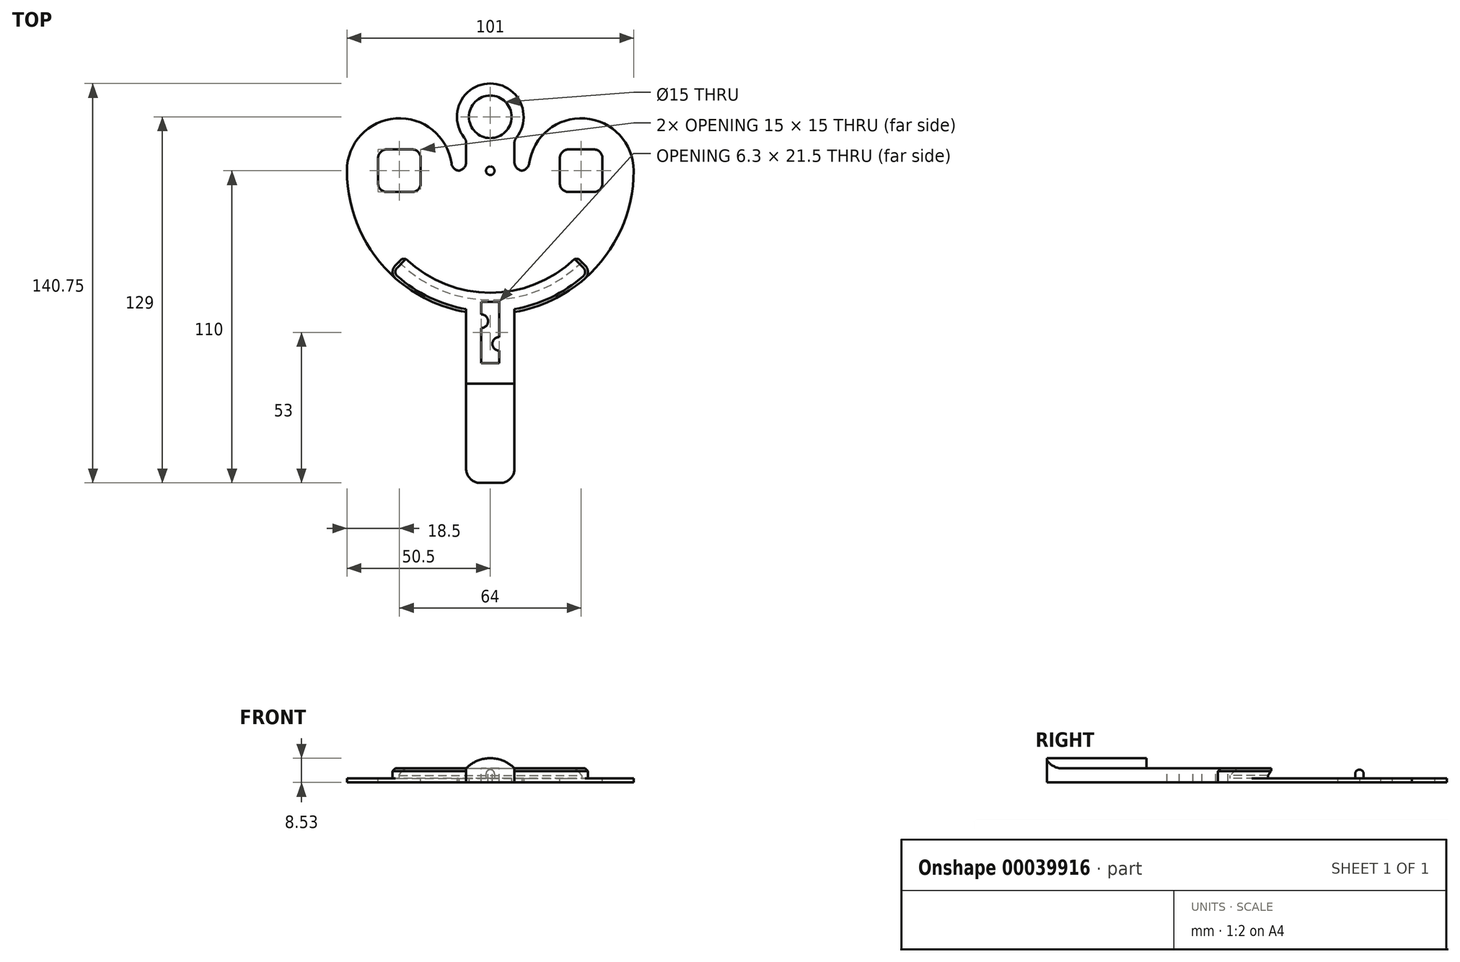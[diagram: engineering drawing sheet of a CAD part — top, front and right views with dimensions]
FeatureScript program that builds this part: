
annotation { "Feature Type Name" : "Feature", "Feature Type Description" : "" }
export const myFeature = defineFeature(function(context is Context, id is Id, definition is map)
    precondition{}
    {
        {
            var Q0;
            Q0=qCreatedBy(makeId("Top.planeOp"),FACE);
            var sketch = newSketch(context, id + "F0", { "sketchPlane" : qUnion([Q0])});
            skLineSegment(sketch, "E0", {"start": v(0, 35) * mm, "end": v(0, -35) * mm, "construction": true});
            skLineSegment(sketch, "E1", {"start": v(-8.5, -40) * mm, "end": v(-8.5, -110) * mm});
            skLineSegment(sketch, "E2", {"start": v(-8.5, -110) * mm, "end": v(0, -110) * mm});
            skLineSegment(sketch, "E3.MirrorCS", {"start": v(8.5, -40) * mm, "end": v(8.5, -110) * mm});
            skLineSegment(sketch, "E4.MirrorCS", {"start": v(8.5, -110) * mm, "end": v(0, -110) * mm});
            skEllipse(sketch, "E5.0", {"center": v(0, 0) * mm, "majorRadius": 67.5 * mm, "minorRadius": 35 * mm, "majorAxis": v(1, 0), "construction": true});
            skCircle(sketch, "E6.0", {"center": v(-32, 0) * mm, "radius": 17.5 * mm, "construction": true});
            skCircle(sketch, "E7.0", {"center": v(32, 0) * mm, "radius": 17.5 * mm, "construction": true});
            skLineSegment(sketch, "E8", {"start": v(0, -110) * mm, "end": v(0, -40) * mm, "construction": true});
            skLineSegment(sketch, "E9", {"start": v(0, -35) * mm, "end": v(0, -40) * mm, "construction": true});
            skLineSegment(sketch, "E10", {"start": v(-8.5, -40) * mm, "end": v(8.5, -40) * mm});
            skSolve(sketch);
        }
        {
            var Q0;
            Q0=qSketchRegion(id+"F0",true);
            extrude(context, id + "F1", {"entities" : qUnion([Q0]), "depth" : 5 * mm});
        }
        {
            var Q0;
            Q0=makeQuery(id+"F1.opExtrude","CAP_FACE",FACE,{"disambiguationData":[OSD([sQuery(id+"F0.wireOp",EDGE,"7391e9a9-ae98-415e-9696-a7713fd930ae"),sQuery(id+"F0.wireOp",EDGE,"7767e17a-6af5-4bc8-a544-19a58f6916b8"),sQuery(id+"F0.wireOp",EDGE,"E1"),sQuery(id+"F0.wireOp",EDGE,"E2"),sQuery(id+"F0.wireOp",EDGE,"69639bf5-fd83-4191-99ff-23f08a1ee2360.MirrorCS"),sQuery(id+"F0.wireOp",EDGE,"e829f9c4-7dbb-4f23-9f44-d63990e1826a0.MirrorCS"),sQuery(id+"F0.wireOp",EDGE,"E3.MirrorCS"),sQuery(id+"F0.wireOp",EDGE,"E4.MirrorCS")])],"isStart":false});
            var sketch = newSketch(context, id + "F2", { "sketchPlane" : qUnion([Q0])});
            skLineSegment(sketch, "E11", {"start": v(0, 0) * mm, "end": v(0, -57) * mm, "construction": true});
            skLineSegment(sketch, "E12.rect.bottom", {"start": v(3.15, -67.75) * mm, "end": v(-3.15, -67.75) * mm});
            skLineSegment(sketch, "E12.rect.top", {"start": v(3.15, -46.25) * mm, "end": v(-3.15, -46.25) * mm});
            skLineSegment(sketch, "E12.rect.left", {"start": v(3.15, -67.75) * mm, "end": v(3.15, -46.25) * mm, "construction": true});
            skLineSegment(sketch, "E12.rect.right", {"start": v(-3.15, -67.75) * mm, "end": v(-3.15, -46.25) * mm, "construction": true});
            skPoint(sketch, "E12.rect.middle", {"position": v(0, -57) * mm});
            skLineSegment(sketch, "E13", {"start": v(-3.15, -46.25) * mm, "end": v(-3.15, -50.6) * mm});
            skArc(sketch, "E14", {"start": v(-3.15, -55.4) * mm, "mid": v(-0.75, -53) * mm, "end": v(-3.15, -50.6) * mm});
            skLineSegment(sketch, "E15", {"start": v(-3.15, -53) * mm, "end": v(-3.15, -46.25) * mm, "construction": true});
            skLineSegment(sketch, "E16", {"start": v(-3.15, -55.4) * mm, "end": v(-3.15, -67.75) * mm});
            skLineSegment(sketch, "E17", {"start": v(3.15, -67.75) * mm, "end": v(3.15, -63.4) * mm});
            skArc(sketch, "E18", {"start": v(3.15, -58.6) * mm, "mid": v(0.75, -61) * mm, "end": v(3.15, -63.4) * mm});
            skLineSegment(sketch, "E19", {"start": v(3.15, -58.6) * mm, "end": v(3.15, -46.25) * mm});
            skLineSegment(sketch, "E20", {"start": v(-3.15, -53) * mm, "end": v(-3.15, -57) * mm, "construction": true});
            skLineSegment(sketch, "E21", {"start": v(-3.15, -57) * mm, "end": v(0, -57) * mm, "construction": true});
            skLineSegment(sketch, "E22", {"start": v(3.15, -61) * mm, "end": v(3.15, -57) * mm, "construction": true});
            skSolve(sketch);
        }
        {
            var Q0;
            Q0=qSketchRegion(id+"F2",true);
            extrude(context, id + "F3", {"entities" : qUnion([Q0]), "operationType" : NewBodyOperationType.REMOVE, "endBound" : BoundingType.THROUGH_ALL, "oppositeDirection" : true, "depth" : 140 * mm});
        }
        {
            var Q0;
            Q0=makeQuery(id+"F1.opExtrude","SWEPT_FACE",FACE,{"disambiguationData":[OSD([sQuery(id+"F0.wireOp",EDGE,"E2"),sQuery(id+"F0.wireOp",EDGE,"E4.MirrorCS")])]});
            var sketch = newSketch(context, id + "F4", { "sketchPlane" : qUnion([Q0])});
            skLineSegment(sketch, "E23", {"start": v(-8.5, 5) * mm, "end": v(8.5, 5) * mm});
            skArc(sketch, "E24", {"start": v(8.5, 5) * mm, "mid": v(0, 8.53) * mm, "end": v(-8.5, 5) * mm});
            skSolve(sketch);
        }
        {
            var Q0;
            Q0=qSketchRegion(id+"F4",true);
            extrude(context, id + "F5", {"entities" : qUnion([Q0]), "operationType" : NewBodyOperationType.ADD, "oppositeDirection" : true, "depth" : 35 * mm});
        }
        {
            var Q0;
            Q0=makeQuery(id+"F5.opExtrude","CAP_EDGE",EDGE,{"disambiguationData":[OSD([sQuery(id+"F4.wireOp",EDGE,"E23")])],"isStart":false});
            var Q1;
            Q1=makeQuery(id+"FVXrfRP8fz1N6uW_1.boolean.opBoolean","INTERSECT",EDGE,{"derivedFrom":[makeQuery(id+"F1.opExtrude","SWEPT_FACE",FACE,{"disambiguationData":[OSD([sQuery(id+"F0.wireOp",EDGE,"E1")])]}),makeQuery(id+"FVXrfRP8fz1N6uW_1.opExtrude","SWEPT_FACE",FACE,{"disambiguationData":[OSD([sQuery(id+"FPdbJcEM4c8p8f5_1.wireOp",EDGE,"055e796a-4696-4a1f-8bd5-7584a93b29ed.right")])]})]});
            var Q2;
            Q2=makeQuery(id+"FVXrfRP8fz1N6uW_1.boolean.opBoolean","INTERSECT",EDGE,{"derivedFrom":[makeQuery(id+"F1.opExtrude","SWEPT_FACE",FACE,{"disambiguationData":[OSD([sQuery(id+"F0.wireOp",EDGE,"E3.MirrorCS")])]}),makeQuery(id+"FVXrfRP8fz1N6uW_1.opExtrude","SWEPT_FACE",FACE,{"disambiguationData":[OSD([sQuery(id+"FPdbJcEM4c8p8f5_1.wireOp",EDGE,"055e796a-4696-4a1f-8bd5-7584a93b29ed.right")])]})]});
            var Q3;
            Q3=makeQuery(id+"F1.opExtrude","SWEPT_EDGE",EDGE,{"disambiguationData":[OSD([sQuery(id+"F0.wireOp",EDGE,"E1"),sQuery(id+"F0.wireOp",EDGE,"E2")])]});
            var Q4;
            Q4=makeQuery(id+"F1.opExtrude","SWEPT_EDGE",EDGE,{"disambiguationData":[OSD([sQuery(id+"F0.wireOp",EDGE,"E3.MirrorCS"),sQuery(id+"F0.wireOp",EDGE,"E4.MirrorCS")])]});
            fillet(context, id + "F6", {"entities" : qUnion([Q0, Q1, Q2, Q3, Q4]), "radius" : 5 * mm, "tangentPropagation" : true, "allowEdgeOverflow" : false});
        }
        {
            var Q0;
            Q0=qCreatedBy(makeId("Top.planeOp"),FACE);
            var sketch = newSketch(context, id + "F7", { "sketchPlane" : qUnion([Q0])});
            skCircle(sketch, "E25", {"center": v(0, 0) * mm, "radius": 32 * mm, "construction": true});
            skPoint(sketch, "E26.0", {"position": v(32, 0) * mm});
            skPoint(sketch, "E27.0", {"position": v(-8.5, -40) * mm});
            skPoint(sketch, "E28.0", {"position": v(8.5, -40) * mm});
            skLineSegment(sketch, "E29.bottom", {"start": v(-8.5, -40) * mm, "end": v(8.5, -40) * mm});
            skLineSegment(sketch, "E29.top", {"start": v(-8.5, 0) * mm, "end": v(8.5, 0) * mm, "construction": true});
            skLineSegment(sketch, "E29.left", {"start": v(-8.5, -40) * mm, "end": v(-8.5, 0) * mm});
            skLineSegment(sketch, "E29.right", {"start": v(8.5, -40) * mm, "end": v(8.5, 0) * mm});
            skLineSegment(sketch, "E30", {"start": v(0, 0) * mm, "end": v(0, 19) * mm, "construction": true});
            skCircle(sketch, "E31", {"center": v(0, 19) * mm, "radius": 7.5 * mm});
            skCircle(sketch, "E32", {"center": v(0, 19) * mm, "radius": 11.75 * mm});
            skLineSegment(sketch, "E33.top", {"start": v(-8.5, 10.9) * mm, "end": v(8.5, 10.9) * mm, "construction": true});
            skLineSegment(sketch, "E33.left", {"start": v(-8.5, 0) * mm, "end": v(-8.5, 10.9) * mm});
            skLineSegment(sketch, "E33.right", {"start": v(8.5, 0) * mm, "end": v(8.5, 10.9) * mm});
            skLineSegment(sketch, "E34", {"start": v(0, 7.25) * mm, "end": v(0, 11.5) * mm, "construction": true});
            skSolve(sketch);
        }
        {
            var Q0;
            Q0 = qSketchRegion(id + "F7", true);
            extrude(context, id + "F8", {"entities" : qUnion([Q0]), "operationType" : NewBodyOperationType.ADD, "depth" : 5 * mm});
        }
        {
            var Q0;
            Q0=makeQuery(id+"F8.boolean.opBoolean","MERGE",FACE,{"derivedFrom":[makeQuery(id+"F1.opExtrude","CAP_FACE",FACE,{"disambiguationData":[OSD([sQuery(id+"F0.wireOp",EDGE,"E1"),sQuery(id+"F0.wireOp",EDGE,"E2"),sQuery(id+"F0.wireOp",EDGE,"E3.MirrorCS"),sQuery(id+"F0.wireOp",EDGE,"E4.MirrorCS"),sQuery(id+"F0.wireOp",EDGE,"E10")])],"isStart":false}),makeQuery(id+"F8.opExtrude","CAP_FACE",FACE,{"disambiguationData":[OSD([sQuery(id+"F7.wireOp",EDGE,"E29.bottom"),sQuery(id+"F7.wireOp",EDGE,"E29.left"),sQuery(id+"F7.wireOp",EDGE,"E29.right"),sQuery(id+"F7.wireOp",EDGE,"d812d8d3-a707-410c-a5e6-c5c524671fea")])],"isStart":false})]});
            var sketch = newSketch(context, id + "F9", { "sketchPlane" : qUnion([Q0])});
            skCircle(sketch, "E35", {"center": v(0, 0) * mm, "radius": 45.5 * mm});
            skSolve(sketch);
        }
        {
            var Q0;
            Q0 = qSketchRegion(id + "F9", true);
            extrude(context, id + "F10", {"entities" : qUnion([Q0]), "operationType" : NewBodyOperationType.REMOVE, "oppositeDirection" : true, "depth" : 3.5 * mm});
        }
        {
            var Q0;
            Q0=qCreatedBy(makeId("Top.planeOp"),FACE);
            var sketch = newSketch(context, id + "F11", { "sketchPlane" : qUnion([Q0])});
            skCircle(sketch, "E36.0", {"center": v(0, 0) * mm, "radius": 45.5 * mm, "construction": true});
            skArc(sketch, "E37", {"start": v(-45.5, 0) * mm, "mid": v(0, -45.5) * mm, "end": v(45.5, 0) * mm, "construction": true});
            skArc(sketch, "E38.0", {"start": v(-50.5, 0) * mm, "mid": v(0, -50.5) * mm, "end": v(50.5, 0) * mm});
            skPoint(sketch, "E39.0", {"position": v(-32, 0) * mm});
            skArc(sketch, "E40", {"start": v(-13.5, 0) * mm, "mid": v(-32, 18.5) * mm, "end": v(-50.5, 0) * mm});
            skArc(sketch, "E41.MirrorCS", {"start": v(13.5, 0) * mm, "mid": v(32, 18.5) * mm, "end": v(50.5, 0) * mm});
            skLineSegment(sketch, "E42", {"start": v(-13.5, 0) * mm, "end": v(13.5, 0) * mm});
            skSolve(sketch);
        }
        {
            var Q0;
            Q0=makeQuery(id+"F11.imprint","IMPRINT",FACE,{"disambiguationData":[TD([[makeQuery(id+"F11.imprint","IMPRINT",EDGE,{"derivedFrom":sQuery(id+"F11.wireOp",EDGE,"E38.0")}),1.0]])]});
            extrude(context, id + "F12", {"entities" : qUnion([Q0]), "operationType" : NewBodyOperationType.ADD, "depth" : 1.5 * mm});
        }
        {
            var Q0;
            Q0=makeQuery(id+"F12.boolean.opBoolean","MERGE",FACE,{"derivedFrom":[makeQuery(id+"F10.boolean.opBoolean","COPY",FACE,{"derivedFrom":makeQuery(id+"F10.opExtrude","CAP_FACE",FACE,{"disambiguationData":[OSD([sQuery(id+"F9.wireOp",EDGE,"E35")])],"isStart":false})}),makeQuery(id+"F12.opExtrude","CAP_FACE",FACE,{"disambiguationData":[OSD([sQuery(id+"F11.wireOp",EDGE,"E38.0"),sQuery(id+"F11.wireOp",EDGE,"07fb357d-3f39-45c2-a34c-5d68cf75340c")])],"isStart":false})]});
            var sketch = newSketch(context, id + "F13", { "sketchPlane" : qUnion([Q0])});
            skLineSegment(sketch, "E43", {"start": v(-50.5, 0) * mm, "end": v(-50.5, 0) * mm});
            skArc(sketch, "E44.0", {"start": v(-32.17, -32.17) * mm, "mid": v(0, -45.5) * mm, "end": v(32.17, -32.17) * mm});
            skPoint(sketch, "E45.0", {"position": v(-8.5, -44.7) * mm});
            skArc(sketch, "E46", {"start": v(-35.7, -35.7) * mm, "mid": v(0, -50.5) * mm, "end": v(35.7, -35.7) * mm});
            skLineSegment(sketch, "E47", {"start": v(0, 0) * mm, "end": v(-35.7, -35.7) * mm, "construction": true});
            skLineSegment(sketch, "E48.MirrorCS", {"start": v(0, 0) * mm, "end": v(35.7, -35.7) * mm, "construction": true});
            skLineSegment(sketch, "E49", {"start": v(-35.7, -35.7) * mm, "end": v(-32.17, -32.17) * mm});
            skLineSegment(sketch, "E50", {"start": v(35.7, -35.7) * mm, "end": v(32.17, -32.17) * mm});
            skSolve(sketch);
        }
        {
            var Q0;
            Q0 = qSketchRegion(id + "F13", true);
            extrude(context, id + "F14", {"entities" : qUnion([Q0]), "operationType" : NewBodyOperationType.ADD, "depth" : 3.5 * mm});
        }
        {
            var Q0;
            Q0=makeQuery(id+"F14.opExtrude","CAP_VERTEX",VERTEX,{"disambiguationData":[OSD([sQuery(id+"F13.wireOp",EDGE,"E44.0"),sQuery(id+"F13.wireOp",EDGE,"E49")])],"isStart":false});
            var Q1;
            Q1=makeQuery(id+"F14.boolean.opBoolean","MERGE",EDGE,{"derivedFrom":[makeQuery(id+"F10.boolean.opBoolean","COPY",EDGE,{"derivedFrom":makeQuery(id+"F10.opExtrude","CAP_EDGE",EDGE,{"disambiguationData":[OSD([sQuery(id+"F9.wireOp",EDGE,"E35")])],"isStart":true})}),makeQuery(id+"F14.opExtrude","CAP_EDGE",EDGE,{"disambiguationData":[OSD([sQuery(id+"F13.wireOp",EDGE,"E44.0")])],"isStart":false})]});
            cPlane(context, id + "F15", {"entities" : qUnion([Q0, Q1]), "cplaneType" : CPlaneType.CURVE_POINT, "offset" : 150 * mm, "width" : 150 * mm, "height" : 150 * mm});
        }
        {
            var Q0;
            Q0=qCreatedBy(id+"F15.planeOp",FACE);
            var sketch = newSketch(context, id + "F16", { "sketchPlane" : qUnion([Q0])});
            skPoint(sketch, "E51.0", {"position": v(-45.5, 5) * mm});
            skLineSegment(sketch, "E52", {"start": v(-45.5, 5) * mm, "end": v(-45.5, 2.5) * mm});
            skLineSegment(sketch, "E53", {"start": v(-45.5, 2.5) * mm, "end": v(-43, 5) * mm});
            skLineSegment(sketch, "E54", {"start": v(-43, 5) * mm, "end": v(-45.5, 5) * mm});
            skSolve(sketch);
        }
        {
            var Q0;
            Q0=makeQuery(id+"F16.imprint","IMPRINT",FACE,{"disambiguationData":[TD([[makeQuery(id+"F16.imprint","IMPRINT",EDGE,{"derivedFrom":sQuery(id+"F16.wireOp",EDGE,"E52")}),1.0]])]});
            var Q1;
            Q1=makeQuery(id+"F14.boolean.opBoolean","MERGE",EDGE,{"derivedFrom":[makeQuery(id+"F10.boolean.opBoolean","COPY",EDGE,{"derivedFrom":makeQuery(id+"F10.opExtrude","CAP_EDGE",EDGE,{"disambiguationData":[OSD([sQuery(id+"F9.wireOp",EDGE,"E35")])],"isStart":true})}),makeQuery(id+"F14.opExtrude","CAP_EDGE",EDGE,{"disambiguationData":[OSD([sQuery(id+"F13.wireOp",EDGE,"E44.0")])],"isStart":false})]});
            sweep(context, id + "F17", {"operationType" : NewBodyOperationType.ADD, "profiles" : qUnion([Q0]), "path" : qUnion([Q1])});
        }
        {
            var Q0;
            Q0=makeQuery(id+"F12.boolean.opBoolean","MERGE",FACE,{"derivedFrom":[makeQuery(id+"F10.boolean.opBoolean","COPY",FACE,{"derivedFrom":makeQuery(id+"F10.opExtrude","CAP_FACE",FACE,{"disambiguationData":[OSD([sQuery(id+"F9.wireOp",EDGE,"E35")])],"isStart":false})}),makeQuery(id+"F12.opExtrude","CAP_FACE",FACE,{"disambiguationData":[OSD([sQuery(id+"F11.wireOp",EDGE,"E38.0"),sQuery(id+"F11.wireOp",EDGE,"E40"),sQuery(id+"F11.wireOp",EDGE,"E41.MirrorCS"),sQuery(id+"F11.wireOp",EDGE,"E42")])],"isStart":false})]});
            var sketch = newSketch(context, id + "F18", { "sketchPlane" : qUnion([Q0])});
            skLineSegment(sketch, "E55.rect.bottom", {"start": v(-24.5, -7.5) * mm, "end": v(-39.5, -7.5) * mm});
            skLineSegment(sketch, "E55.rect.top", {"start": v(-24.5, 7.5) * mm, "end": v(-39.5, 7.5) * mm});
            skLineSegment(sketch, "E55.rect.left", {"start": v(-24.5, -7.5) * mm, "end": v(-24.5, 7.5) * mm});
            skLineSegment(sketch, "E55.rect.right", {"start": v(-39.5, -7.5) * mm, "end": v(-39.5, 7.5) * mm});
            skPoint(sketch, "E55.rect.middle", {"position": v(-32, 0) * mm});
            skLineSegment(sketch, "E56.rect.bottom", {"start": v(24.5, -7.5) * mm, "end": v(39.5, -7.5) * mm});
            skLineSegment(sketch, "E56.rect.top", {"start": v(24.5, 7.5) * mm, "end": v(39.5, 7.5) * mm});
            skLineSegment(sketch, "E56.rect.left", {"start": v(24.5, -7.5) * mm, "end": v(24.5, 7.5) * mm});
            skLineSegment(sketch, "E56.rect.right", {"start": v(39.5, -7.5) * mm, "end": v(39.5, 7.5) * mm});
            skPoint(sketch, "E56.rect.middle", {"position": v(32, 0) * mm});
            skSolve(sketch);
        }
        {
            var Q0;
            Q0 = qSketchRegion(id + "F18", true);
            extrude(context, id + "F19", {"entities" : qUnion([Q0]), "operationType" : NewBodyOperationType.REMOVE, "endBound" : BoundingType.THROUGH_ALL, "oppositeDirection" : true, "depth" : 25 * mm});
        }
        {
            var Q0;
            Q0=makeQuery(id+"F2.imprint","IMPRINT",FACE,{"disambiguationData":[TD([[makeQuery(id+"F2.imprint","IMPRINT",EDGE,{"derivedFrom":sQuery(id+"F2.wireOp",EDGE,"E12.rect.bottom")}),-1.0]])]});
            extrude(context, id + "F20", {"entities" : qUnion([Q0]), "operationType" : NewBodyOperationType.REMOVE, "endBound" : BoundingType.THROUGH_ALL, "oppositeDirection" : true, "depth" : 25 * mm});
        }
        {
            var Q0;
            Q0=makeQuery(id+"F12.boolean.opBoolean","MERGE",FACE,{"derivedFrom":[makeQuery(id+"F10.boolean.opBoolean","COPY",FACE,{"derivedFrom":makeQuery(id+"F10.opExtrude","CAP_FACE",FACE,{"disambiguationData":[OSD([sQuery(id+"F9.wireOp",EDGE,"E35")])],"isStart":false})}),makeQuery(id+"F12.opExtrude","CAP_FACE",FACE,{"disambiguationData":[OSD([sQuery(id+"F11.wireOp",EDGE,"E38.0"),sQuery(id+"F11.wireOp",EDGE,"E40"),sQuery(id+"F11.wireOp",EDGE,"E41.MirrorCS"),sQuery(id+"F11.wireOp",EDGE,"E42")])],"isStart":false})]});
            var sketch = newSketch(context, id + "F21", { "sketchPlane" : qUnion([Q0])});
            skCircle(sketch, "E57", {"center": v(0, 0) * mm, "radius": 1.5 * mm});
            skSolve(sketch);
        }
        {
            var Q0;
            Q0 = qSketchRegion(id + "F21", true);
            extrude(context, id + "F22", {"entities" : qUnion([Q0]), "operationType" : NewBodyOperationType.ADD, "depth" : 3 * mm});
        }
        {
            var Q0;
            Q0=makeQuery(id+"F12.opExtrude","SWEPT_EDGE",EDGE,{"disambiguationData":[OSD([sQuery(id+"F11.wireOp",EDGE,"E40"),sQuery(id+"F11.wireOp",EDGE,"E42")])]});
            var Q1;
            Q1=makeQuery(id+"F12.opExtrude","SWEPT_EDGE",EDGE,{"disambiguationData":[OSD([sQuery(id+"F11.wireOp",EDGE,"E41.MirrorCS"),sQuery(id+"F11.wireOp",EDGE,"E42")])]});
            var Q2;
            Q2=makeQuery(id+"F19.boolean.opBoolean","COPY",EDGE,{"derivedFrom":makeQuery(id+"F19.opExtrude","SWEPT_EDGE",EDGE,{"disambiguationData":[OSD([sQuery(id+"F18.wireOp",EDGE,"E56.rect.bottom"),sQuery(id+"F18.wireOp",EDGE,"E56.rect.right")])]})});
            var Q3;
            Q3=makeQuery(id+"F19.boolean.opBoolean","COPY",EDGE,{"derivedFrom":makeQuery(id+"F19.opExtrude","SWEPT_EDGE",EDGE,{"disambiguationData":[OSD([sQuery(id+"F18.wireOp",EDGE,"E56.rect.bottom"),sQuery(id+"F18.wireOp",EDGE,"E56.rect.left")])]})});
            var Q4;
            Q4=makeQuery(id+"F19.boolean.opBoolean","COPY",EDGE,{"derivedFrom":makeQuery(id+"F19.opExtrude","SWEPT_EDGE",EDGE,{"disambiguationData":[OSD([sQuery(id+"F18.wireOp",EDGE,"E56.rect.top"),sQuery(id+"F18.wireOp",EDGE,"E56.rect.left")])]})});
            var Q5;
            Q5=makeQuery(id+"F19.boolean.opBoolean","COPY",EDGE,{"derivedFrom":makeQuery(id+"F19.opExtrude","SWEPT_EDGE",EDGE,{"disambiguationData":[OSD([sQuery(id+"F18.wireOp",EDGE,"E56.rect.top"),sQuery(id+"F18.wireOp",EDGE,"E56.rect.right")])]})});
            var Q6;
            Q6=makeQuery(id+"F19.boolean.opBoolean","COPY",EDGE,{"derivedFrom":makeQuery(id+"F19.opExtrude","SWEPT_EDGE",EDGE,{"disambiguationData":[OSD([sQuery(id+"F18.wireOp",EDGE,"E55.rect.top"),sQuery(id+"F18.wireOp",EDGE,"E55.rect.left")])]})});
            var Q7;
            Q7=makeQuery(id+"F19.boolean.opBoolean","COPY",EDGE,{"derivedFrom":makeQuery(id+"F19.opExtrude","SWEPT_EDGE",EDGE,{"disambiguationData":[OSD([sQuery(id+"F18.wireOp",EDGE,"E55.rect.bottom"),sQuery(id+"F18.wireOp",EDGE,"E55.rect.right")])]})});
            var Q8;
            Q8=makeQuery(id+"F19.boolean.opBoolean","COPY",EDGE,{"derivedFrom":makeQuery(id+"F19.opExtrude","SWEPT_EDGE",EDGE,{"disambiguationData":[OSD([sQuery(id+"F18.wireOp",EDGE,"E55.rect.bottom"),sQuery(id+"F18.wireOp",EDGE,"E55.rect.left")])]})});
            var Q9;
            Q9=makeQuery(id+"F19.boolean.opBoolean","COPY",EDGE,{"derivedFrom":makeQuery(id+"F19.opExtrude","SWEPT_EDGE",EDGE,{"disambiguationData":[OSD([sQuery(id+"F18.wireOp",EDGE,"E55.rect.top"),sQuery(id+"F18.wireOp",EDGE,"E55.rect.right")])]})});
            var Q10;
            Q10=makeQuery(id+"F12.boolean.opBoolean","INTERSECT",EDGE,{"derivedFrom":[makeQuery(id+"F8.boolean.opBoolean","MERGE",FACE,{"derivedFrom":[makeQuery(id+"F1.opExtrude","SWEPT_FACE",FACE,{"disambiguationData":[OSD([sQuery(id+"F0.wireOp",EDGE,"E3.MirrorCS")])]}),makeQuery(id+"F8.opExtrude","SWEPT_FACE",FACE,{"disambiguationData":[OSD([sQuery(id+"F7.wireOp",EDGE,"E29.right"),sQuery(id+"F7.wireOp",EDGE,"E33.right")])]})]}),makeQuery(id+"F12.opExtrude","SWEPT_FACE",FACE,{"disambiguationData":[OSD([sQuery(id+"F11.wireOp",EDGE,"E42")])]})]});
            var Q11;
            Q11=makeQuery(id+"F12.boolean.opBoolean","INTERSECT",EDGE,{"derivedFrom":[makeQuery(id+"F8.boolean.opBoolean","MERGE",FACE,{"derivedFrom":[makeQuery(id+"F1.opExtrude","SWEPT_FACE",FACE,{"disambiguationData":[OSD([sQuery(id+"F0.wireOp",EDGE,"E1")])]}),makeQuery(id+"F8.opExtrude","SWEPT_FACE",FACE,{"disambiguationData":[OSD([sQuery(id+"F7.wireOp",EDGE,"E29.left"),sQuery(id+"F7.wireOp",EDGE,"E33.left")])]})]}),makeQuery(id+"F12.opExtrude","SWEPT_FACE",FACE,{"disambiguationData":[OSD([sQuery(id+"F11.wireOp",EDGE,"E42")])]})]});
            var Q12;
            Q12=makeQuery(id+"F8.opExtrude","SWEPT_EDGE",EDGE,{"disambiguationData":[OSD([sQuery(id+"F7.wireOp",EDGE,"E32"),sQuery(id+"F7.wireOp",EDGE,"E33.left")])]});
            var Q13;
            Q13=makeQuery(id+"F8.opExtrude","SWEPT_EDGE",EDGE,{"disambiguationData":[OSD([sQuery(id+"F7.wireOp",EDGE,"E32"),sQuery(id+"F7.wireOp",EDGE,"E33.right")])]});
            var Q14;
            Q14=makeQuery(id+"F14.opExtrude","SWEPT_EDGE",EDGE,{"disambiguationData":[OSD([sQuery(id+"F11.wireOp",EDGE,"E41.MirrorCS"),sQuery(id+"F13.wireOp",EDGE,"5365c932-d4e2-4f65-8009-f3c9c269d2c60.MirrorCS"),sQuery(id+"F13.wireOp",EDGE,"E46")])]});
            var Q15;
            Q15=makeQuery(id+"F14.opExtrude","SWEPT_EDGE",EDGE,{"disambiguationData":[OSD([sQuery(id+"F11.wireOp",EDGE,"E40"),sQuery(id+"F13.wireOp",EDGE,"f397ccce-6ca3-4197-a77e-3b8086db523c"),sQuery(id+"F13.wireOp",EDGE,"E46")])]});
            fillet(context, id + "F23", {"entities" : qUnion([Q0, Q1, Q2, Q3, Q4, Q5, Q6, Q7, Q8, Q9, Q10, Q11, Q12, Q13, Q14, Q15]), "radius" : 3 * mm, "tangentPropagation" : true, "allowEdgeOverflow" : false});
        }
        {
            var Q0;
            Q0=makeQuery(id+"F22.opExtrude","CAP_EDGE",EDGE,{"disambiguationData":[OSD([sQuery(id+"F21.wireOp",EDGE,"E57")])],"isStart":false});
            fillet(context, id + "F24", {"entities" : qUnion([Q0]), "radius" : 1.5 * mm, "tangentPropagation" : true, "allowEdgeOverflow" : false});
        }
        {
            var Q0;
            {var subQ0=sQuery(id+"F13.wireOp",EDGE,"f397ccce-6ca3-4197-a77e-3b8086db523c");Q0=makeQuery(id+"F17.boolean.opBoolean","MERGE",EDGE,{"derivedFrom":[makeQuery(id+"F14.opExtrude","CAP_EDGE",EDGE,{"disambiguationData":[OSD([subQ0])],"isStart":false}),makeQuery(id+"F17.opSweep","CAP_EDGE",EDGE,{"disambiguationData":[OSD([sQuery(id+"F13.wireOp",EDGE,"E44.0"),subQ0,sQuery(id+"F16.wireOp",EDGE,"E54")])],"isStart":true})]});}
            var Q1;
            {var subQ0=sQuery(id+"F13.wireOp",EDGE,"5365c932-d4e2-4f65-8009-f3c9c269d2c60.MirrorCS");Q1=makeQuery(id+"F17.boolean.opBoolean","MERGE",EDGE,{"derivedFrom":[makeQuery(id+"F14.opExtrude","CAP_EDGE",EDGE,{"disambiguationData":[OSD([subQ0])],"isStart":false}),makeQuery(id+"F17.opSweep","CAP_EDGE",EDGE,{"disambiguationData":[OSD([sQuery(id+"F13.wireOp",EDGE,"E44.0"),subQ0,sQuery(id+"F16.wireOp",EDGE,"E54")])],"isStart":false})]});}
            chamfer(context, id + "F25", {"entities" : qUnion([Q0, Q1]), "width" : 1 * mm, "tangentPropagation" : true});
        }
    });
